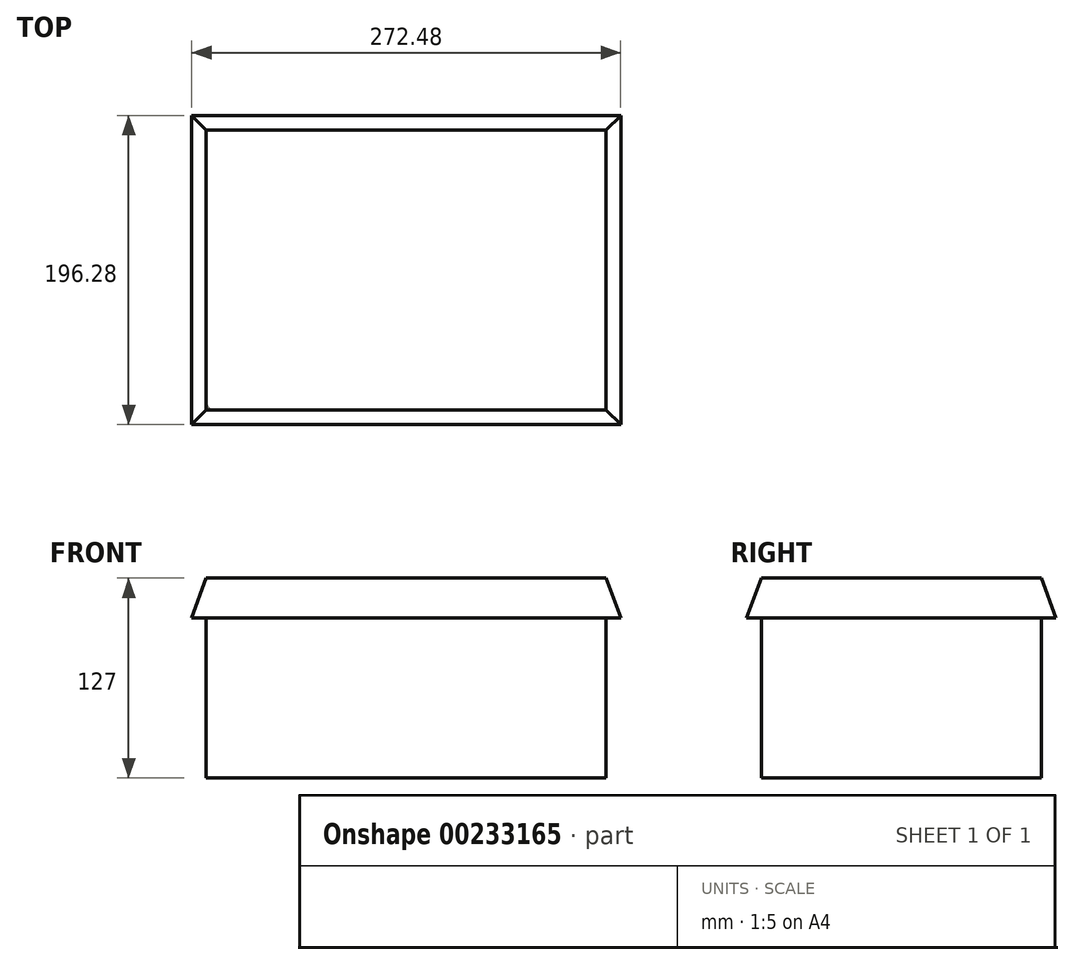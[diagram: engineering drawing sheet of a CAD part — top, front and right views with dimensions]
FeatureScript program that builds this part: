
annotation { "Feature Type Name" : "Feature", "Feature Type Description" : "" }
export const myFeature = defineFeature(function(context is Context, id is Id, definition is map)
    precondition{}
    {
        {
            var Q0;
            Q0=qCreatedBy(makeId("Top.planeOp"),FACE);
            var sketch = newSketch(context, id + "F0", { "sketchPlane" : qUnion([Q0])});
            skLineSegment(sketch, "E0.bottom", {"start": v(-127, 88.9) * mm, "end": v(127, 88.9) * mm});
            skLineSegment(sketch, "E0.top", {"start": v(-127, -88.9) * mm, "end": v(127, -88.9) * mm});
            skLineSegment(sketch, "E0.left", {"start": v(-127, 88.9) * mm, "end": v(-127, -88.9) * mm});
            skLineSegment(sketch, "E0.right", {"start": v(127, 88.9) * mm, "end": v(127, -88.9) * mm});
            skSolve(sketch);
        }
        {
            var Q0;
            Q0=makeQuery(id+"F0.imprint","IMPRINT",FACE,{"disambiguationData":[TD([[makeQuery(id+"F0.imprint","IMPRINT",EDGE,{"derivedFrom":sQuery(id+"F0.wireOp",EDGE,"E0.bottom")}),-1.0]])]});
            extrude(context, id + "F1", {"entities" : qUnion([Q0]), "depth" : 127 * mm});
        }
        {
            var Q0;
            Q0=makeQuery(id+"F1.opExtrude","CAP_FACE",FACE,{"disambiguationData":[OSD([sQuery(id+"F0.wireOp",EDGE,"E0.bottom"),sQuery(id+"F0.wireOp",EDGE,"E0.top"),sQuery(id+"F0.wireOp",EDGE,"E0.left"),sQuery(id+"F0.wireOp",EDGE,"E0.right")])],"isStart":false});
            extrude(context, id + "F2", {"entities" : qUnion([Q0]), "operationType" : NewBodyOperationType.ADD, "oppositeDirection" : true, "depth" : 25.4 * mm, "hasDraft" : true, "draftAngle" : 20 * degree});
        }
        {
            var Q0;
            Q0=makeQuery(id+"F1.opExtrude","SWEPT_EDGE",EDGE,{"disambiguationData":[OSD([sQuery(id+"F0.wireOp",EDGE,"E0.top"),sQuery(id+"F0.wireOp",EDGE,"E0.left")])]});
            fillet(context, id + "F3", {"entities" : qUnion([Q0]), "radius" : 5.08 * mm, "tangentPropagation" : true, "allowEdgeOverflow" : false});
        }
    });
